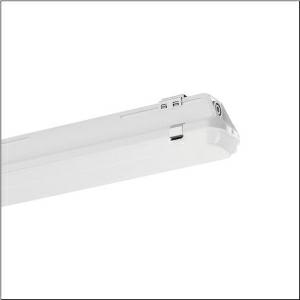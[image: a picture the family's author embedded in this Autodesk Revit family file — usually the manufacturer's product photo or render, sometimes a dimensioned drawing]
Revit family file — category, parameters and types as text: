
# Revit family: monsun_11_51fp12mp4b0u
name_source: partatom
category: Lighting Fixtures
units: mm (PartAtom-declared; Revit-internal decimal feet)

## family parameters
Cut with Voids When Loaded = No
Host = Face
Light Source = No
Part Type = Normal
Room Calculation Point = No
Round Connector Dimension = Use Diameter
Shared = No

## types (1)
- --- (1 x LED, 11850 lm, 62.4 W, 4000K)
    Apparent Load = 62 VA
    CIE Flux Codes = 62 86 96 97 100
    Color Rendering = 80
    Color Temperature = 4000K
    Default Elevation = 1800 mm
    Description = Monsun 11, damp-proof luminaire, chain hanger, primary light control with lens, primary optical cover: enclosure, of PMMA, light emission: direct distribution, primary light characteristic: symmetric, installation type: suspended mounting, surface-mounted, horizontal mounting, vertical mounting, LED, rated luminous flux: 11.850lm, luminous efficacy: 190lm/W, light colour: 840, colour temperature: 4000K, control gear: ON/OFF Multilumen, with terminal, 3-pole, max. 2.5mm², mains connection: 220..240V, AC, 50/60Hz, rated input power: 62W, luminaire housing, of glass-fibre reinforced polyester, uncoated, bright grey, incl. chain hanger, length: 1.590mm, width: 90mm, height: 88mm, clip for enclosure, of stainless steel (V2A), ceiling mounting element, of stainless steel (V2A), chain hanger, of stainless steel (V2A), protection rating (complete): IP66, insulation class (complete): insulation class I (protective earthing), certification: CE, ENEC, VDE, UKCA, protection symbol: D, impact resistance: IK04, permissible operating ambient temperature: -35..+35°C, standard: EN 50419, EN 60598-2-1, contact your sales advisor before using the luminaires in applications with unclear chemical exposure, large temperature fluctuations or condensation-forming humidity, LABS conformity tested according to VDMA 24364:2018-05, no direct snow, no direct sun, no direct rain, for indoor or canopied outdoor use, corresponds to IFS (International Featured Standards) requirements for safety and quality in the food industry, packaging unit: 1 piece
    Height = 89 mm
    Lamp = 1 x LED
    Lamp Light Flux = 11850 lm
    Lamp Power = 62.4 W
    Lamp count = 1
    Length = 1590 mm
    Luminous efficacy = 190 lm/W
    Manufacturer = Siteco
    ModVariant = No
    Model = 51FP12MP4B0U
    Mounting Place = Ceiling
    Mounting Type = Surface mounted
    Number of Poles = 1
    OnlyDefault = Yes
    Power Factor = 1
    Product Name = Monsun 11
    Product group = damp-proof luminaire
    ProductGroupID = 300
    Protection Class = Protection class I
    Protection Degree = IP 66
    RLX_Detail_Level = 1
    RLX_Emergency_Light_Flux = 0 lm
    RLX_Emergency_Type = 0
    RLX_Emergency_Type_DB = No
    RlxData = <blob elided: 90013 chars, md5=975137a9>
    Socket = socket
    Standby Power = 0 W
    System Light Flux = 11850 lm
    System Power = 62 W
    Type Comments = factory setting: luminous flux: 100 % | (A | C | E) | 147 mA
    Type Image = l_1349237.jpg
    URL = http://relux.com
    VarID = @adj_000049
    Voltage = 0 V
    Weight = 0.00 kg
    Width = 90 mm

## geometry (parser evidence)
native form markers: Blend x4, Sweep x10
no freeform markers — native parametric forms only
